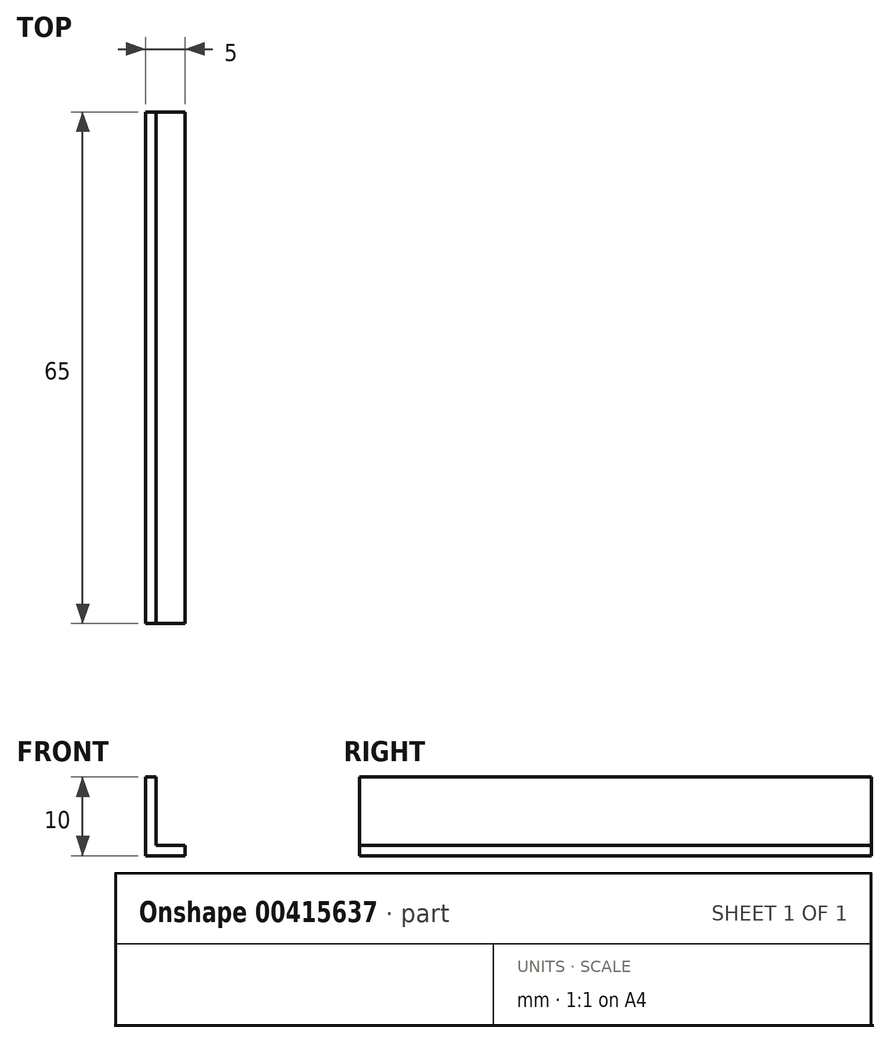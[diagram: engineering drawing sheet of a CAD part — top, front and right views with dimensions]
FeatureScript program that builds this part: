
annotation { "Feature Type Name" : "Feature", "Feature Type Description" : "" }
export const myFeature = defineFeature(function(context is Context, id is Id, definition is map)
    precondition{}
    {
        {
            var Q0;
            Q0=qCreatedBy(makeId("Front.planeOp"),FACE);
            var sketch = newSketch(context, id + "F0", { "sketchPlane" : qUnion([Q0])});
            skLineSegment(sketch, "E0", {"start": v(-4.53, 12.4) * mm, "end": v(-4.53, 2.4) * mm});
            skLineSegment(sketch, "E1", {"start": v(-4.53, 2.4) * mm, "end": v(0.47, 2.4) * mm});
            skLineSegment(sketch, "E2", {"start": v(0.47, 2.4) * mm, "end": v(0.47, 3.7) * mm});
            skLineSegment(sketch, "E3", {"start": v(0.47, 3.7) * mm, "end": v(-3.23, 3.7) * mm});
            skLineSegment(sketch, "E4", {"start": v(-3.23, 3.7) * mm, "end": v(-3.23, 12.4) * mm});
            skLineSegment(sketch, "E5", {"start": v(-3.23, 12.4) * mm, "end": v(-4.53, 12.4) * mm});
            skSolve(sketch);
        }
        {
            var Q0;
            Q0=makeQuery(id+"F0.imprint","IMPRINT",FACE,{"disambiguationData":[TD([[makeQuery(id+"F0.imprint","IMPRINT",EDGE,{"derivedFrom":sQuery(id+"F0.wireOp",EDGE,"E0")}),1.0]])]});
            extrude(context, id + "F1", {"entities" : qUnion([Q0]), "depth" : 65 * mm});
        }
    });
